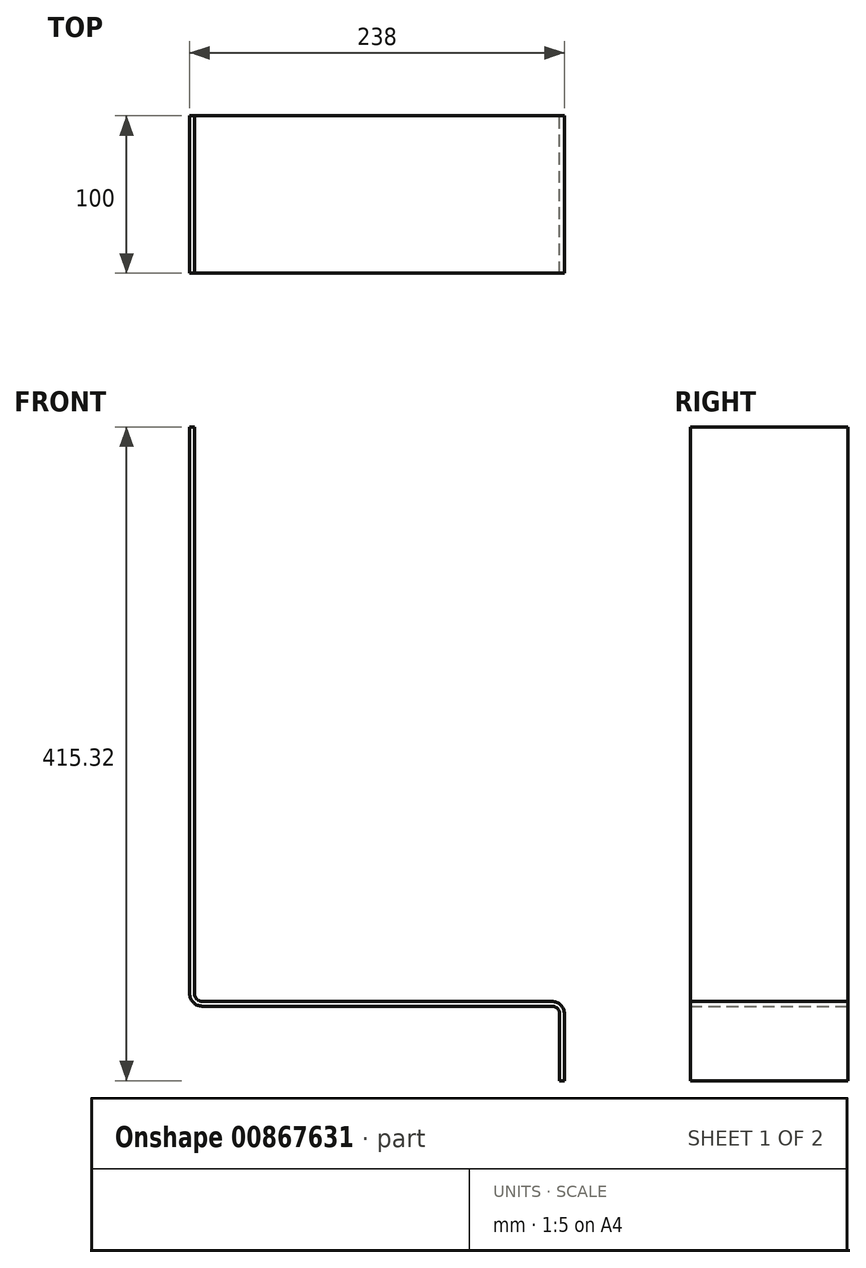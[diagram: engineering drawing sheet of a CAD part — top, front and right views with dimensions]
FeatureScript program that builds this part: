
annotation { "Feature Type Name" : "Feature", "Feature Type Description" : "" }
export const myFeature = defineFeature(function(context is Context, id is Id, definition is map)
    precondition{}
    {
        {
            var Q0;
            Q0=qCreatedBy(makeId("Front.planeOp"),FACE);
            var sketch = newSketch(context, id + "F0", { "sketchPlane" : qUnion([Q0])});
            skArc(sketch, "E0", {"start": v(-5, 0) * mm, "mid": v(-3.54, -3.54) * mm, "end": v(0, -5) * mm});
            skLineSegment(sketch, "E1", {"start": v(-5, 0) * mm, "end": v(-5, 360) * mm});
            skLineSegment(sketch, "E2", {"start": v(0, -5) * mm, "end": v(222, -5) * mm});
            skLineSegment(sketch, "E3", {"start": v(230, -13) * mm, "end": v(230, -55.32) * mm});
            skLineSegment(sketch, "E4", {"start": v(230, -55.32) * mm, "end": v(227, -55.32) * mm});
            skLineSegment(sketch, "E5", {"start": v(227, -55.32) * mm, "end": v(227, -13) * mm});
            skLineSegment(sketch, "E6", {"start": v(-5, 360) * mm, "end": v(-8, 360) * mm});
            skLineSegment(sketch, "E7", {"start": v(-8, 360) * mm, "end": v(-8, -3) * mm});
            skArc(sketch, "E8", {"start": v(-8, 0) * mm, "mid": v(-5.66, -5.66) * mm, "end": v(0, -8) * mm});
            skLineSegment(sketch, "E9", {"start": v(0, -8) * mm, "end": v(222, -8) * mm});
            skPoint(sketch, "E10", {"position": v(222, -13) * mm});
            skArc(sketch, "E11", {"start": v(227, -13) * mm, "mid": v(225.54, -9.46) * mm, "end": v(222, -8) * mm});
            skArc(sketch, "E12", {"start": v(230, -13) * mm, "mid": v(227.66, -7.34) * mm, "end": v(222, -5) * mm});
            skSolve(sketch);
        }
        {
            var Q0;
            Q0=makeQuery(id+"F0.imprint","IMPRINT",FACE,{"disambiguationData":[TD([[makeQuery(id+"F0.imprint","IMPRINT",EDGE,{"derivedFrom":sQuery(id+"F0.wireOp",EDGE,"E0")}),-1.0]])]});
            extrude(context, id + "F1", {"entities" : qUnion([Q0]), "depth" : 100 * mm, "offsetDistance" : 25 * mm});
        }
    });
